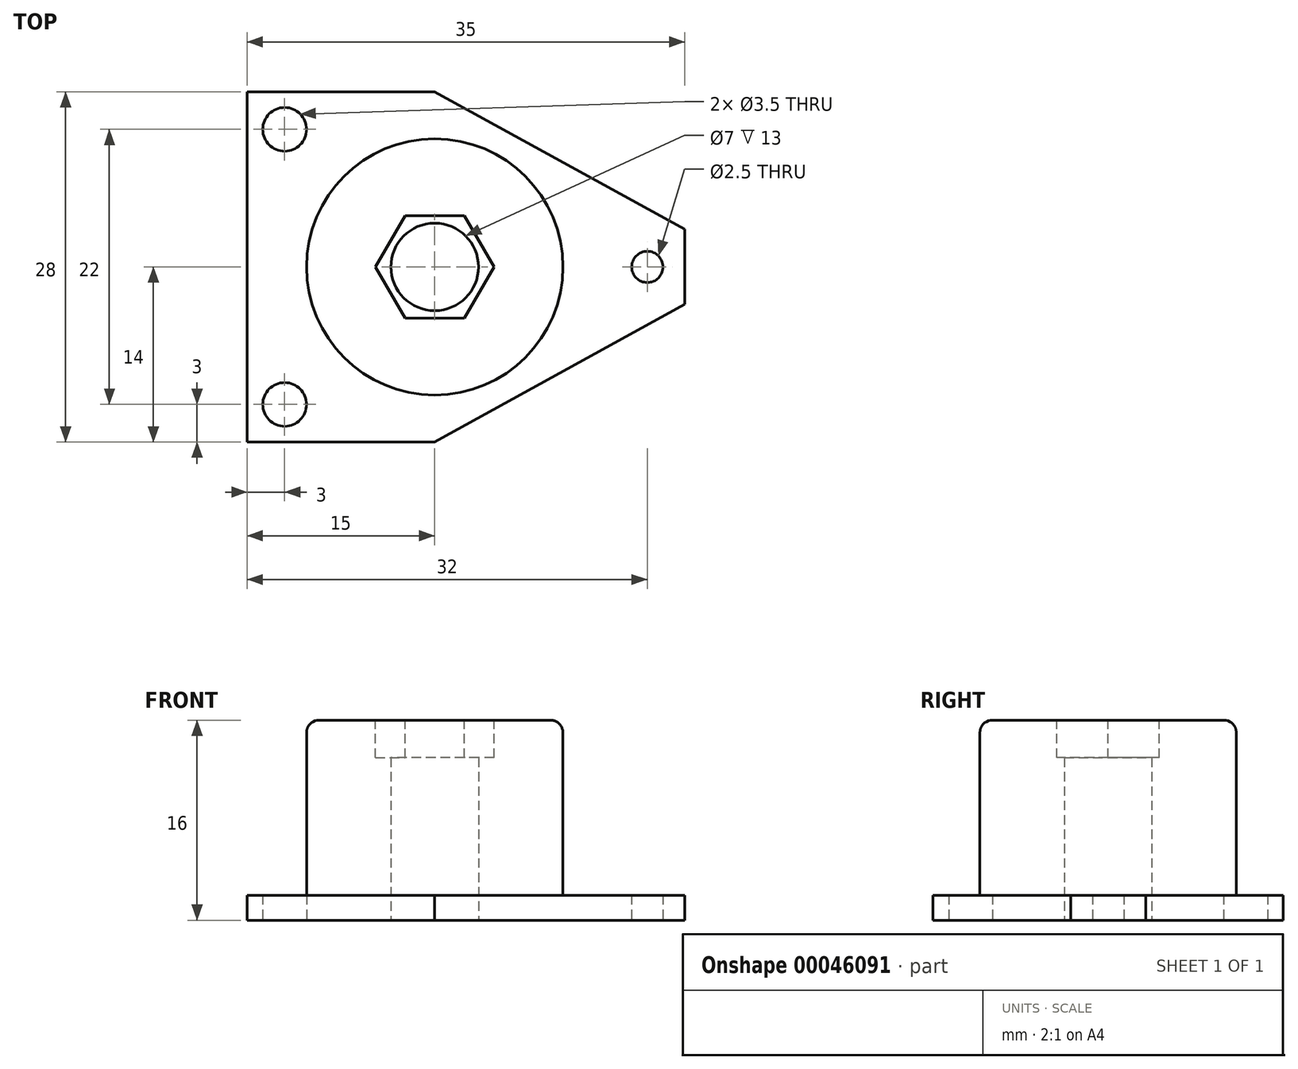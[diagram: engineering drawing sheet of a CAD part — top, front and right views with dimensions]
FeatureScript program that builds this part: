
annotation { "Feature Type Name" : "Feature", "Feature Type Description" : "" }
export const myFeature = defineFeature(function(context is Context, id is Id, definition is map)
    precondition{}
    {
        {
            var Q0;
            Q0=qCreatedBy(makeId("Top.planeOp"),FACE);
            var sketch = newSketch(context, id + "F0", { "sketchPlane" : qUnion([Q0])});
            skCircle(sketch, "E0", {"center": v(0, 0) * mm, "radius": 3.5 * mm});
            skLineSegment(sketch, "E1.bottom", {"start": v(-15, 14) * mm, "end": v(0, 14) * mm});
            skLineSegment(sketch, "E1.top", {"start": v(-15, -14) * mm, "end": v(0, -14) * mm});
            skLineSegment(sketch, "E1.left", {"start": v(-15, 14) * mm, "end": v(-15, -14) * mm});
            skLineSegment(sketch, "E1.right", {"start": v(0, 14) * mm, "end": v(0, -14) * mm});
            skLineSegment(sketch, "E2", {"start": v(0, 0) * mm, "end": v(20, 0) * mm, "construction": true});
            skCircle(sketch, "E3", {"center": v(-12, 11) * mm, "radius": 1.75 * mm});
            skCircle(sketch, "E4.MirrorC", {"center": v(-12, -11) * mm, "radius": 1.75 * mm});
            skCircle(sketch, "E5", {"center": v(17, 0) * mm, "radius": 1.25 * mm});
            skLineSegment(sketch, "E6", {"start": v(20, 0) * mm, "end": v(20, 3) * mm});
            skLineSegment(sketch, "E7", {"start": v(20, 3) * mm, "end": v(0, 14) * mm});
            skLineSegment(sketch, "E8.MirrorCS", {"start": v(20, -3) * mm, "end": v(0, -14) * mm});
            skLineSegment(sketch, "E9.MirrorCS", {"start": v(20, 0) * mm, "end": v(20, -3) * mm});
            skSolve(sketch);
        }
        {
            var Q0;
            Q0 = qSketchRegion(id + "F0", true);
            extrude(context, id + "F1", {"entities" : qUnion([Q0]), "depth" : 2 * mm});
        }
        {
            var Q0;
            Q0=makeQuery(id+"F1.opExtrude","CAP_FACE",FACE,{"disambiguationData":[OSD([sQuery(id+"F0.wireOp",EDGE,"E0"),sQuery(id+"F0.wireOp",EDGE,"E1.bottom"),sQuery(id+"F0.wireOp",EDGE,"E1.top"),sQuery(id+"F0.wireOp",EDGE,"E1.left"),sQuery(id+"F0.wireOp",EDGE,"E3"),sQuery(id+"F0.wireOp",EDGE,"E4.MirrorC"),sQuery(id+"F0.wireOp",EDGE,"E5"),sQuery(id+"F0.wireOp",EDGE,"E6"),sQuery(id+"F0.wireOp",EDGE,"E7"),sQuery(id+"F0.wireOp",EDGE,"E8.MirrorCS"),sQuery(id+"F0.wireOp",EDGE,"E9.MirrorCS")])],"isStart":false});
            var sketch = newSketch(context, id + "F2", { "sketchPlane" : qUnion([Q0])});
            skCircle(sketch, "E10", {"center": v(0, 0) * mm, "radius": 10.25 * mm});
            skSolve(sketch);
        }
        {
            var Q0;
            Q0=makeQuery(id+"F2.imprint","IMPRINT",FACE,{"disambiguationData":[TD([[makeQuery(id+"F2.imprint","IMPRINT",EDGE,{"derivedFrom":sQuery(id+"F2.wireOp",EDGE,"E10")}),1.0]])]});
            extrude(context, id + "F3", {"entities" : qUnion([Q0]), "operationType" : NewBodyOperationType.ADD, "depth" : 14 * mm});
        }
        {
            var Q0;
            Q0=makeQuery(id+"F3.opExtrude","CAP_FACE",FACE,{"disambiguationData":[OSD([sQuery(id+"F0.wireOp",EDGE,"E0"),sQuery(id+"F2.wireOp",EDGE,"E10")])],"isStart":false});
            var sketch = newSketch(context, id + "F4", { "sketchPlane" : qUnion([Q0])});
            skCircle(sketch, "E11.cCircle", {"center": v(0, 0) * mm, "radius": 4.1 * mm, "construction": true});
            skLineSegment(sketch, "E11.0", {"start": v(2.37, -4.1) * mm, "end": v(-2.37, -4.1) * mm});
            skLineSegment(sketch, "E11.1", {"start": v(-2.37, -4.1) * mm, "end": v(-4.73, 0) * mm});
            skLineSegment(sketch, "E11.2", {"start": v(-4.73, 0) * mm, "end": v(-2.37, 4.1) * mm});
            skLineSegment(sketch, "E11.3", {"start": v(-2.37, 4.1) * mm, "end": v(2.37, 4.1) * mm});
            skLineSegment(sketch, "E11.4", {"start": v(2.37, 4.1) * mm, "end": v(4.73, 0) * mm});
            skLineSegment(sketch, "E11.5", {"start": v(4.73, 0) * mm, "end": v(2.37, -4.1) * mm});
            skPoint(sketch, "E11.0.midPoint", {"position": v(0, -4.1) * mm});
            skSolve(sketch);
        }
        {
            var Q0;
            Q0=makeQuery(id+"F4.imprint","IMPRINT",FACE,{"disambiguationData":[TD([[makeQuery(id+"F4.imprint","IMPRINT",EDGE,{"derivedFrom":sQuery(id+"F4.wireOp",EDGE,"E11.0")}),-1.0]])]});
            extrude(context, id + "F5", {"entities" : qUnion([Q0]), "operationType" : NewBodyOperationType.REMOVE, "oppositeDirection" : true, "depth" : 3 * mm});
        }
        {
            var Q0;
            Q0=makeQuery(id+"F5.boolean.opBoolean","COPY",EDGE,{"derivedFrom":makeQuery(id+"F5.opExtrude","CAP_EDGE",EDGE,{"disambiguationData":[OSD([sQuery(id+"F4.wireOp",EDGE,"E11.2")])],"isStart":true})});
            var Q1;
            Q1=makeQuery(id+"F5.boolean.opBoolean","COPY",EDGE,{"derivedFrom":makeQuery(id+"F5.opExtrude","CAP_EDGE",EDGE,{"disambiguationData":[OSD([sQuery(id+"F4.wireOp",EDGE,"E11.3")])],"isStart":true})});
            var Q2;
            Q2=makeQuery(id+"F5.boolean.opBoolean","COPY",EDGE,{"derivedFrom":makeQuery(id+"F5.opExtrude","CAP_EDGE",EDGE,{"disambiguationData":[OSD([sQuery(id+"F4.wireOp",EDGE,"E11.4")])],"isStart":true})});
            var Q3;
            Q3=makeQuery(id+"F5.boolean.opBoolean","COPY",EDGE,{"derivedFrom":makeQuery(id+"F5.opExtrude","CAP_EDGE",EDGE,{"disambiguationData":[OSD([sQuery(id+"F4.wireOp",EDGE,"E11.5")])],"isStart":true})});
            var Q4;
            Q4=makeQuery(id+"F5.boolean.opBoolean","COPY",EDGE,{"derivedFrom":makeQuery(id+"F5.opExtrude","CAP_EDGE",EDGE,{"disambiguationData":[OSD([sQuery(id+"F4.wireOp",EDGE,"E11.0")])],"isStart":true})});
            var Q5;
            Q5=makeQuery(id+"F5.boolean.opBoolean","COPY",EDGE,{"derivedFrom":makeQuery(id+"F5.opExtrude","CAP_EDGE",EDGE,{"disambiguationData":[OSD([sQuery(id+"F4.wireOp",EDGE,"E11.1")])],"isStart":true})});
            var Q6;
            Q6=makeQuery(id+"F3.opExtrude","CAP_EDGE",EDGE,{"disambiguationData":[OSD([sQuery(id+"F2.wireOp",EDGE,"E10")])],"isStart":false});
            fillet(context, id + "F6", {"entities" : qUnion([Q0, Q1, Q2, Q3, Q4, Q5, Q6]), "radius" : 1 * mm, "tangentPropagation" : true, "allowEdgeOverflow" : false});
        }
    });
